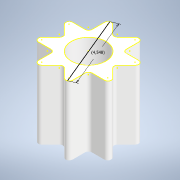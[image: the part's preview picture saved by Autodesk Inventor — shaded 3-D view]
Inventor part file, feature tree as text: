
AUTODESK INVENTOR PART (.ipt)
format: ipt  version: 2022.3 (Build 263350000, 350)  size: 382,976 bytes
history: native  units: mm
features: extrude x8, sketch x7, imported_body x4, projected_geometry x2
ambient origin geometry x8: Origin, YZ Plane, XZ Plane, XY Plane, X Axis, Y Axis, Z Axis, Center Point
bodies: Solid1 (feature_tree), Solid2 (feature_tree), Solid3 (feature_tree), Solid4 (feature_tree)
feature tree (21):
  sketch  "Sketch1"  dims[d0=0.0mm d1=0.0mm d2=10.0mm d3=0.0mm]
  extrude  "Extrusion1"  Depth=10.0mm TaperAngle=0.0deg
  extrude  "Extrusion2"  Depth=10.0mm TaperAngle=0.0deg
  extrude  "Extrusion3"  Depth=10.0mm TaperAngle=0.0deg
  extrude  "Extrusion4"  Depth=10.0mm
  extrude  "Extrusion5"  [1 undecoded]
  extrude  "Extrusion6"  [1 undecoded]
  extrude  "Extrusion7"  [1 undecoded]
  extrude  "Extrusion8"  [1 undecoded]
  projected_geometry  "Projected Loop1"
  sketch  "Sketch2"  dims[d4=10.0mm d5=0.0mm d6=10.0mm d7=0.0mm]
  sketch  "Sketch3"  dims[d8=10.0mm d9=0.0mm d10=10.0mm d11=0.0mm]
  sketch  "Sketch4"  dims[d12=10.0mm d13=0.0mm d14=2.0mm]
  sketch  "Sketch5"  dims[d15=10.0mm d16=0.0mm]
  sketch  "Sketch6"
  projected_geometry  "Projected Loop2"
  sketch  "Sketch7"
  imported_body  "Base1"
  imported_body  "Base2"
  imported_body  "Base3"
  imported_body  "Base4"
note: 4 required parameter values undecoded (feature->parameter linkage not recoverable at this tier; creation-order binding heuristic only, values carry confidence <= 0.55)
